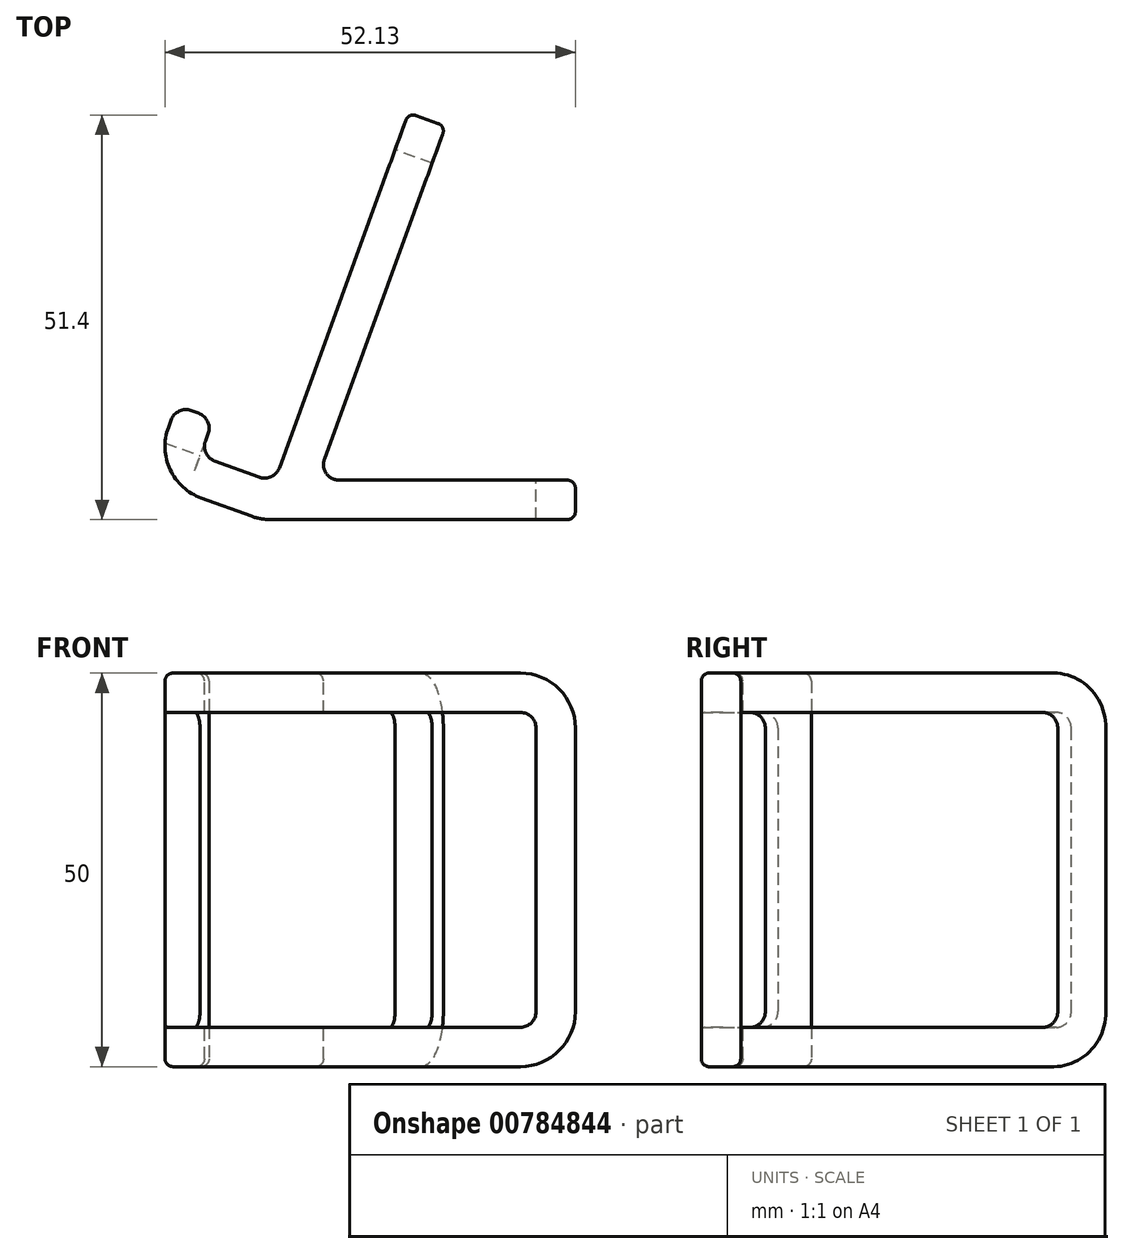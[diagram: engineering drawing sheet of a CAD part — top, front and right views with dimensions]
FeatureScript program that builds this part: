
annotation { "Feature Type Name" : "Feature", "Feature Type Description" : "" }
export const myFeature = defineFeature(function(context is Context, id is Id, definition is map)
    precondition{}
    {
        {
            var Q0;
            Q0=qCreatedBy(makeId("Top.planeOp"),FACE);
            var sketch = newSketch(context, id + "F0", { "sketchPlane" : qUnion([Q0])});
            skLineSegment(sketch, "E0", {"start": v(17.1, 46.98) * mm, "end": v(0, 0) * mm});
            skLineSegment(sketch, "E1", {"start": v(0, 0) * mm, "end": v(-9.4, 3.42) * mm});
            skLineSegment(sketch, "E2", {"start": v(38.29, -4.7) * mm, "end": v(38.29, 0.3) * mm});
            skLineSegment(sketch, "E3", {"start": v(38.29, 0.3) * mm, "end": v(5.43, 0.3) * mm});
            skLineSegment(sketch, "E4", {"start": v(5.43, 0.3) * mm, "end": v(21.8, 45.27) * mm});
            skLineSegment(sketch, "E5", {"start": v(21.8, 45.27) * mm, "end": v(17.1, 46.98) * mm});
            skLineSegment(sketch, "E6", {"start": v(-9.4, 3.42) * mm, "end": v(-7.69, 8.12) * mm});
            skLineSegment(sketch, "E7", {"start": v(-7.69, 8.12) * mm, "end": v(-12.39, 9.83) * mm});
            skLineSegment(sketch, "E8", {"start": v(-12.39, 9.83) * mm, "end": v(-15.8, 0.43) * mm});
            skLineSegment(sketch, "E9", {"start": v(-15.8, 0.43) * mm, "end": v(-1.71, -4.7) * mm});
            skLineSegment(sketch, "E10", {"start": v(-1.71, -4.7) * mm, "end": v(38.29, -4.7) * mm});
            skLineSegment(sketch, "E11", {"start": v(0, 0) * mm, "end": v(0, 50) * mm, "construction": true});
            skLineSegment(sketch, "E12", {"start": v(0, 0) * mm, "end": v(54.72, 150.35) * mm, "construction": true});
            skPoint(sketch, "E13", {"position": v(27.36, 75.18) * mm});
            skLineSegment(sketch, "E14", {"start": v(27.36, 75.18) * mm, "end": v(27.36, -4.7) * mm, "construction": true});
            skSolve(sketch);
        }
        {
            var Q0;
            Q0=makeQuery(id+"F0.imprint","IMPRINT",FACE,{"disambiguationData":[TD([[makeQuery(id+"F0.imprint","IMPRINT",EDGE,{"derivedFrom":sQuery(id+"F0.wireOp",EDGE,"E0")}),1.0]])]});
            extrude(context, id + "F1", {"entities" : qUnion([Q0]), "depth" : 50 * mm, "offsetDistance" : 25 * mm});
        }
        {
            var Q0;
            Q0=makeQuery(id+"F1.opExtrude","SWEPT_FACE",FACE,{"disambiguationData":[OSD([sQuery(id+"F0.wireOp",EDGE,"E0")])]});
            var sketch = newSketch(context, id + "F2", { "sketchPlane" : qUnion([Q0])});
            skLineSegment(sketch, "E15.bottom", {"start": v(-45, 5) * mm, "end": v(5, 5) * mm});
            skLineSegment(sketch, "E15.top", {"start": v(-45, 45) * mm, "end": v(5, 45) * mm});
            skLineSegment(sketch, "E15.left", {"start": v(-45, 5) * mm, "end": v(-45, 45) * mm});
            skLineSegment(sketch, "E15.right", {"start": v(5, 5) * mm, "end": v(5, 45) * mm});
            skSolve(sketch);
        }
        {
            var Q0;
            Q0=makeQuery(id+"F1.opExtrude","SWEPT_FACE",FACE,{"disambiguationData":[OSD([sQuery(id+"F0.wireOp",EDGE,"E3")])]});
            var sketch = newSketch(context, id + "F3", { "sketchPlane" : qUnion([Q0])});
            skLineSegment(sketch, "E16.bottom", {"start": v(-33.29, 5) * mm, "end": v(-5.43, 5) * mm});
            skLineSegment(sketch, "E16.top", {"start": v(-33.29, 45) * mm, "end": v(-5.43, 45) * mm});
            skLineSegment(sketch, "E16.left", {"start": v(-33.29, 5) * mm, "end": v(-33.29, 45) * mm});
            skLineSegment(sketch, "E16.right", {"start": v(-5.43, 5) * mm, "end": v(-5.43, 45) * mm});
            skSolve(sketch);
        }
        {
            var Q0;
            Q0=makeQuery(id+"F1.opExtrude","SWEPT_FACE",FACE,{"disambiguationData":[OSD([sQuery(id+"F0.wireOp",EDGE,"E1")])]});
            var sketch = newSketch(context, id + "F4", { "sketchPlane" : qUnion([Q0])});
            skLineSegment(sketch, "E17.bottom", {"start": v(20, 5) * mm, "end": v(-10, 5) * mm});
            skLineSegment(sketch, "E17.top", {"start": v(20, 45) * mm, "end": v(-10, 45) * mm});
            skLineSegment(sketch, "E17.left", {"start": v(20, 5) * mm, "end": v(20, 45) * mm});
            skLineSegment(sketch, "E17.right", {"start": v(-10, 5) * mm, "end": v(-10, 45) * mm});
            skSolve(sketch);
        }
        {
            var Q0;
            Q0=makeQuery(id+"F3.imprint","IMPRINT",FACE,{"disambiguationData":[TD([[makeQuery(id+"F3.imprint","IMPRINT",EDGE,{"derivedFrom":sQuery(id+"F3.wireOp",EDGE,"E16.bottom")}),1.0]])]});
            extrude(context, id + "F5", {"entities" : qUnion([Q0]), "operationType" : NewBodyOperationType.REMOVE, "endBound" : BoundingType.THROUGH_ALL, "oppositeDirection" : true, "depth" : 26.6 * mm, "offsetDistance" : 25 * mm});
        }
        {
            var Q0;
            Q0=makeQuery(id+"F4.imprint","IMPRINT",FACE,{"disambiguationData":[TD([[makeQuery(id+"F4.imprint","IMPRINT",EDGE,{"derivedFrom":sQuery(id+"F4.wireOp",EDGE,"E17.bottom")}),-1.0]])]});
            extrude(context, id + "F6", {"entities" : qUnion([Q0]), "operationType" : NewBodyOperationType.REMOVE, "endBound" : BoundingType.THROUGH_ALL, "oppositeDirection" : true, "depth" : 25 * mm, "offsetDistance" : 25 * mm});
        }
        {
            var Q0;
            Q0=makeQuery(id+"F2.imprint","IMPRINT",FACE,{"disambiguationData":[TD([[makeQuery(id+"F2.imprint","IMPRINT",EDGE,{"derivedFrom":sQuery(id+"F2.wireOp",EDGE,"E15.bottom")}),1.0]])]});
            var Q1;
            Q1=makeQuery(id+"F1.opExtrude","SWEPT_FACE",FACE,{"disambiguationData":[OSD([sQuery(id+"F0.wireOp",EDGE,"E4")])]});
            extrude(context, id + "F7", {"entities" : qUnion([Q0]), "operationType" : NewBodyOperationType.REMOVE, "oppositeDirection" : true, "depth" : 21.25 * mm, "endBoundEntityFace" : qUnion([Q1]), "offsetDistance" : 25 * mm});
        }
        {
            var Q0;
            {var subQ0=sQuery(id+"F0.wireOp",EDGE,"E9");var subQ1=sQuery(id+"F0.wireOp",EDGE,"E8");Q0=makeQuery(id+"F6.boolean.opBoolean","SPLIT",EDGE,{"disambiguationData":[TD([makeQuery(id+"F5.boolean.opBoolean","COPY",FACE,{"derivedFrom":makeQuery(id+"F5.opExtrude","SWEPT_FACE",FACE,{"disambiguationData":[OSD([sQuery(id+"F3.wireOp",EDGE,"E16.top")])]})})])],"derivedFrom":makeQuery(id+"F1.opExtrude","SWEPT_EDGE",EDGE,{"disambiguationData":[OSD([subQ1,subQ0])]})});}
            var Q1;
            {var subQ0=sQuery(id+"F0.wireOp",EDGE,"E8");var subQ1=sQuery(id+"F0.wireOp",EDGE,"E9");Q1=makeQuery(id+"F6.boolean.opBoolean","SPLIT",EDGE,{"disambiguationData":[TD([makeQuery(id+"F5.boolean.opBoolean","COPY",FACE,{"derivedFrom":makeQuery(id+"F5.opExtrude","SWEPT_FACE",FACE,{"disambiguationData":[OSD([sQuery(id+"F3.wireOp",EDGE,"E16.bottom")])]})})])],"derivedFrom":makeQuery(id+"F1.opExtrude","SWEPT_EDGE",EDGE,{"disambiguationData":[OSD([subQ0,subQ1])]})});}
            var Q2;
            {var subQ0=sQuery(id+"F0.wireOp",EDGE,"E9");var subQ1=sQuery(id+"F0.wireOp",EDGE,"E10");Q2=makeQuery(id+"F6.boolean.opBoolean","SPLIT",EDGE,{"disambiguationData":[TD([makeQuery(id+"F5.boolean.opBoolean","COPY",FACE,{"derivedFrom":makeQuery(id+"F5.opExtrude","SWEPT_FACE",FACE,{"disambiguationData":[OSD([sQuery(id+"F3.wireOp",EDGE,"E16.top")])]})})])],"derivedFrom":makeQuery(id+"F1.opExtrude","SWEPT_EDGE",EDGE,{"disambiguationData":[OSD([subQ0,subQ1])]})});}
            var Q3;
            {var subQ0=sQuery(id+"F0.wireOp",EDGE,"E10");var subQ1=sQuery(id+"F0.wireOp",EDGE,"E9");Q3=makeQuery(id+"F6.boolean.opBoolean","SPLIT",EDGE,{"disambiguationData":[TD([makeQuery(id+"F5.boolean.opBoolean","COPY",FACE,{"derivedFrom":makeQuery(id+"F5.opExtrude","SWEPT_FACE",FACE,{"disambiguationData":[OSD([sQuery(id+"F3.wireOp",EDGE,"E16.bottom")])]})})])],"derivedFrom":makeQuery(id+"F1.opExtrude","SWEPT_EDGE",EDGE,{"disambiguationData":[OSD([subQ1,subQ0])]})});}
            var Q4;
            Q4=makeQuery(id+"F1.opExtrude","CAP_EDGE",EDGE,{"disambiguationData":[OSD([sQuery(id+"F0.wireOp",EDGE,"E5")])],"isStart":true});
            var Q5;
            Q5=makeQuery(id+"F1.opExtrude","CAP_EDGE",EDGE,{"disambiguationData":[OSD([sQuery(id+"F0.wireOp",EDGE,"E5")])],"isStart":false});
            var Q6;
            Q6=makeQuery(id+"F1.opExtrude","CAP_EDGE",EDGE,{"disambiguationData":[OSD([sQuery(id+"F0.wireOp",EDGE,"E2")])],"isStart":true});
            var Q7;
            Q7=makeQuery(id+"F1.opExtrude","CAP_EDGE",EDGE,{"disambiguationData":[OSD([sQuery(id+"F0.wireOp",EDGE,"E2")])],"isStart":false});
            fillet(context, id + "F8", {"entities" : qUnion([Q0, Q1, Q2, Q3, Q4, Q5, Q6, Q7]), "radius" : 7 * mm, "allowEdgeOverflow" : false});
        }
        {
            var Q0;
            Q0=makeQuery(id+"F7.boolean.opBoolean","COPY",EDGE,{"derivedFrom":makeQuery(id+"F7.opExtrude","SWEPT_EDGE",EDGE,{"disambiguationData":[OSD([sQuery(id+"F2.wireOp",EDGE,"E15.top"),sQuery(id+"F2.wireOp",EDGE,"E15.left")])]})});
            var Q1;
            Q1=makeQuery(id+"F7.boolean.opBoolean","COPY",EDGE,{"derivedFrom":makeQuery(id+"F7.opExtrude","SWEPT_EDGE",EDGE,{"disambiguationData":[OSD([sQuery(id+"F2.wireOp",EDGE,"E15.bottom"),sQuery(id+"F2.wireOp",EDGE,"E15.left")])]})});
            var Q2;
            Q2=makeQuery(id+"F5.boolean.opBoolean","COPY",EDGE,{"derivedFrom":makeQuery(id+"F5.opExtrude","SWEPT_EDGE",EDGE,{"disambiguationData":[OSD([sQuery(id+"F3.wireOp",EDGE,"E16.bottom"),sQuery(id+"F3.wireOp",EDGE,"E16.left")])]})});
            var Q3;
            Q3=makeQuery(id+"F5.boolean.opBoolean","COPY",EDGE,{"derivedFrom":makeQuery(id+"F5.opExtrude","SWEPT_EDGE",EDGE,{"disambiguationData":[OSD([sQuery(id+"F3.wireOp",EDGE,"E16.top"),sQuery(id+"F3.wireOp",EDGE,"E16.left")])]})});
            var Q4;
            {var subQ0=sQuery(id+"F0.wireOp",EDGE,"E6");var subQ1=makeQuery(id+"F1.opExtrude","SWEPT_FACE",FACE,{"disambiguationData":[OSD([subQ0])]});var subQ2=sQuery(id+"F0.wireOp",EDGE,"E1");var subQ3=makeQuery(id+"F1.opExtrude","SWEPT_FACE",FACE,{"disambiguationData":[OSD([subQ2])]});Q4=makeQuery(id+"F6.boolean.opBoolean","SPLIT",EDGE,{"disambiguationData":[topologyDisambiguationEdgeConnected([subQ3,subQ1]),TD([makeQuery(id+"F5.boolean.opBoolean","COPY",FACE,{"derivedFrom":makeQuery(id+"F5.opExtrude","SWEPT_FACE",FACE,{"disambiguationData":[OSD([sQuery(id+"F3.wireOp",EDGE,"E16.bottom")])]})})])],"derivedFrom":makeQuery(id+"F1.opExtrude","SWEPT_EDGE",EDGE,{"disambiguationData":[OSD([subQ2,subQ0])]})});}
            var Q5;
            {var subQ0=sQuery(id+"F0.wireOp",EDGE,"E6");var subQ1=makeQuery(id+"F1.opExtrude","SWEPT_FACE",FACE,{"disambiguationData":[OSD([subQ0])]});var subQ2=sQuery(id+"F0.wireOp",EDGE,"E1");var subQ3=makeQuery(id+"F1.opExtrude","SWEPT_FACE",FACE,{"disambiguationData":[OSD([subQ2])]});Q5=makeQuery(id+"F6.boolean.opBoolean","SPLIT",EDGE,{"disambiguationData":[topologyDisambiguationEdgeConnected([subQ3,subQ1]),TD([makeQuery(id+"F5.boolean.opBoolean","COPY",FACE,{"derivedFrom":makeQuery(id+"F5.opExtrude","SWEPT_FACE",FACE,{"disambiguationData":[OSD([sQuery(id+"F3.wireOp",EDGE,"E16.top")])]})})])],"derivedFrom":makeQuery(id+"F1.opExtrude","SWEPT_EDGE",EDGE,{"disambiguationData":[OSD([subQ2,subQ0])]})});}
            var Q6;
            {var subQ0=sQuery(id+"F0.wireOp",EDGE,"E0");var subQ1=makeQuery(id+"F1.opExtrude","SWEPT_FACE",FACE,{"disambiguationData":[OSD([subQ0])]});var subQ2=sQuery(id+"F0.wireOp",EDGE,"E1");var subQ3=makeQuery(id+"F1.opExtrude","SWEPT_FACE",FACE,{"disambiguationData":[OSD([subQ2])]});Q6=makeQuery(id+"F6.boolean.opBoolean","SPLIT",EDGE,{"disambiguationData":[topologyDisambiguationEdgeConnected([subQ1,subQ3]),TD([makeQuery(id+"F5.boolean.opBoolean","COPY",FACE,{"derivedFrom":makeQuery(id+"F5.opExtrude","SWEPT_FACE",FACE,{"disambiguationData":[OSD([sQuery(id+"F3.wireOp",EDGE,"E16.top")])]})})])],"derivedFrom":makeQuery(id+"F1.opExtrude","SWEPT_EDGE",EDGE,{"disambiguationData":[OSD([subQ0,subQ2])]})});}
            var Q7;
            {var subQ0=sQuery(id+"F0.wireOp",EDGE,"E1");var subQ1=makeQuery(id+"F1.opExtrude","SWEPT_FACE",FACE,{"disambiguationData":[OSD([subQ0])]});var subQ3=sQuery(id+"F0.wireOp",EDGE,"E0");var subQ4=makeQuery(id+"F1.opExtrude","SWEPT_FACE",FACE,{"disambiguationData":[OSD([subQ3])]});Q7=makeQuery(id+"F6.boolean.opBoolean","SPLIT",EDGE,{"disambiguationData":[topologyDisambiguationEdgeConnected([subQ4,subQ1]),TD([makeQuery(id+"F5.boolean.opBoolean","COPY",FACE,{"derivedFrom":makeQuery(id+"F5.opExtrude","SWEPT_FACE",FACE,{"disambiguationData":[OSD([sQuery(id+"F3.wireOp",EDGE,"E16.bottom")])]})})])],"derivedFrom":makeQuery(id+"F1.opExtrude","SWEPT_EDGE",EDGE,{"disambiguationData":[OSD([subQ3,subQ0])]})});}
            var Q8;
            {var subQ0=sQuery(id+"F0.wireOp",EDGE,"E4");var subQ1=sQuery(id+"F0.wireOp",EDGE,"E3");Q8=makeQuery(id+"F5.boolean.opBoolean","SPLIT",EDGE,{"disambiguationData":[TD([makeQuery(id+"F5.opExtrude","SWEPT_FACE",FACE,{"disambiguationData":[OSD([sQuery(id+"F3.wireOp",EDGE,"E16.bottom")])]})])],"derivedFrom":makeQuery(id+"F1.opExtrude","SWEPT_EDGE",EDGE,{"disambiguationData":[OSD([subQ1,subQ0])]})});}
            var Q9;
            {var subQ0=sQuery(id+"F0.wireOp",EDGE,"E4");var subQ1=sQuery(id+"F0.wireOp",EDGE,"E3");Q9=makeQuery(id+"F5.boolean.opBoolean","SPLIT",EDGE,{"disambiguationData":[TD([makeQuery(id+"F5.opExtrude","SWEPT_FACE",FACE,{"disambiguationData":[OSD([sQuery(id+"F3.wireOp",EDGE,"E16.top")])]})])],"derivedFrom":makeQuery(id+"F1.opExtrude","SWEPT_EDGE",EDGE,{"disambiguationData":[OSD([subQ1,subQ0])]})});}
            var Q10;
            Q10=makeQuery(id+"F1.opExtrude","SWEPT_EDGE",EDGE,{"disambiguationData":[OSD([sQuery(id+"F0.wireOp",EDGE,"E7"),sQuery(id+"F0.wireOp",EDGE,"E8")])]});
            var Q11;
            Q11=makeQuery(id+"F1.opExtrude","SWEPT_EDGE",EDGE,{"disambiguationData":[OSD([sQuery(id+"F0.wireOp",EDGE,"E6"),sQuery(id+"F0.wireOp",EDGE,"E7")])]});
            fillet(context, id + "F9", {"entities" : qUnion([Q0, Q1, Q2, Q3, Q4, Q5, Q6, Q7, Q8, Q9, Q10, Q11]), "radius" : 2 * mm, "tangentPropagation" : true, "allowEdgeOverflow" : false});
        }
        {
            var Q0;
            {var subQ0=makeQuery(id+"F5.boolean.opBoolean","COPY",FACE,{"derivedFrom":makeQuery(id+"F5.opExtrude","SWEPT_FACE",FACE,{"disambiguationData":[OSD([sQuery(id+"F3.wireOp",EDGE,"E16.top")])]})});var subQ1=sQuery(id+"F4.wireOp",EDGE,"E17.top");var subQ2=makeQuery(id+"F6.opExtrude","CAP_FACE",FACE,{"disambiguationData":[OSD([sQuery(id+"F4.wireOp",EDGE,"E17.bottom"),subQ1,sQuery(id+"F4.wireOp",EDGE,"E17.left"),sQuery(id+"F4.wireOp",EDGE,"E17.right")])],"isStart":true});var subQ3=makeQuery(id+"F6.opExtrude","SWEPT_FACE",FACE,{"disambiguationData":[OSD([subQ1])]});Q0=makeQuery(id+"F6.boolean.opBoolean","COPY",EDGE,{"disambiguationData":[topologyDisambiguationEdgeConnected([subQ0,subQ2,subQ3]),TD([makeQuery(id+"F1.opExtrude","SWEPT_FACE",FACE,{"disambiguationData":[OSD([sQuery(id+"F0.wireOp",EDGE,"E6")])]})])],"derivedFrom":makeQuery(id+"F6.opExtrude","CAP_EDGE",EDGE,{"disambiguationData":[OSD([subQ1])],"isStart":true})});}
            var Q1;
            {var subQ0=makeQuery(id+"F5.boolean.opBoolean","COPY",FACE,{"derivedFrom":makeQuery(id+"F5.opExtrude","SWEPT_FACE",FACE,{"disambiguationData":[OSD([sQuery(id+"F3.wireOp",EDGE,"E16.bottom")])]})});var subQ1=sQuery(id+"F4.wireOp",EDGE,"E17.bottom");var subQ2=makeQuery(id+"F6.opExtrude","SWEPT_FACE",FACE,{"disambiguationData":[OSD([subQ1])]});var subQ3=makeQuery(id+"F6.opExtrude","CAP_FACE",FACE,{"disambiguationData":[OSD([subQ1,sQuery(id+"F4.wireOp",EDGE,"E17.top"),sQuery(id+"F4.wireOp",EDGE,"E17.left"),sQuery(id+"F4.wireOp",EDGE,"E17.right")])],"isStart":true});Q1=makeQuery(id+"F6.boolean.opBoolean","COPY",EDGE,{"disambiguationData":[topologyDisambiguationEdgeConnected([subQ0,subQ2,subQ3]),TD([makeQuery(id+"F1.opExtrude","SWEPT_FACE",FACE,{"disambiguationData":[OSD([sQuery(id+"F0.wireOp",EDGE,"E6")])]})])],"derivedFrom":makeQuery(id+"F6.opExtrude","CAP_EDGE",EDGE,{"disambiguationData":[OSD([subQ1])],"isStart":true})});}
            var Q2;
            {var subQ0=sQuery(id+"F4.wireOp",EDGE,"E17.top");Q2=makeQuery(id+"F9.opFillet","TWEAK_EDGE",EDGE,{"derivedFrom":[makeQuery(id+"F6.boolean.opBoolean","TWEAK_VERTEX",VERTEX,{"derivedFrom":[makeQuery(id+"F1.opExtrude","SWEPT_FACE",FACE,{"disambiguationData":[OSD([sQuery(id+"F0.wireOp",EDGE,"E1")])]}),makeQuery(id+"F1.opExtrude","SWEPT_FACE",FACE,{"disambiguationData":[OSD([sQuery(id+"F0.wireOp",EDGE,"E6")])]}),makeQuery(id+"F5.boolean.opBoolean","COPY",FACE,{"derivedFrom":makeQuery(id+"F5.opExtrude","SWEPT_FACE",FACE,{"disambiguationData":[OSD([sQuery(id+"F3.wireOp",EDGE,"E16.top")])]})}),makeQuery(id+"F6.opExtrude","CAP_FACE",FACE,{"disambiguationData":[OSD([sQuery(id+"F4.wireOp",EDGE,"E17.bottom"),subQ0,sQuery(id+"F4.wireOp",EDGE,"E17.left"),sQuery(id+"F4.wireOp",EDGE,"E17.right")])],"isStart":true}),makeQuery(id+"F6.opExtrude","SWEPT_FACE",FACE,{"disambiguationData":[OSD([subQ0])]})]})]});}
            var Q3;
            {var subQ0=sQuery(id+"F4.wireOp",EDGE,"E17.bottom");Q3=makeQuery(id+"F9.opFillet","TWEAK_EDGE",EDGE,{"derivedFrom":[makeQuery(id+"F6.boolean.opBoolean","TWEAK_VERTEX",VERTEX,{"derivedFrom":[makeQuery(id+"F1.opExtrude","SWEPT_FACE",FACE,{"disambiguationData":[OSD([sQuery(id+"F0.wireOp",EDGE,"E1")])]}),makeQuery(id+"F1.opExtrude","SWEPT_FACE",FACE,{"disambiguationData":[OSD([sQuery(id+"F0.wireOp",EDGE,"E6")])]}),makeQuery(id+"F5.boolean.opBoolean","COPY",FACE,{"derivedFrom":makeQuery(id+"F5.opExtrude","SWEPT_FACE",FACE,{"disambiguationData":[OSD([sQuery(id+"F3.wireOp",EDGE,"E16.bottom")])]})}),makeQuery(id+"F6.opExtrude","SWEPT_FACE",FACE,{"disambiguationData":[OSD([subQ0])]}),makeQuery(id+"F6.opExtrude","CAP_FACE",FACE,{"disambiguationData":[OSD([subQ0,sQuery(id+"F4.wireOp",EDGE,"E17.top"),sQuery(id+"F4.wireOp",EDGE,"E17.left"),sQuery(id+"F4.wireOp",EDGE,"E17.right")])],"isStart":true})]})]});}
            fillet(context, id + "F10", {"entities" : qUnion([Q0, Q1, Q2, Q3]), "radius" : 2 * mm, "tangentPropagation" : true, "allowEdgeOverflow" : false});
        }
        {
            var Q0;
            Q0=makeQuery(id+"F5.boolean.opBoolean","COPY",EDGE,{"derivedFrom":makeQuery(id+"F5.opExtrude","CAP_EDGE",EDGE,{"disambiguationData":[OSD([sQuery(id+"F3.wireOp",EDGE,"E16.left")])],"isStart":true})});
            var Q1;
            Q1=makeQuery(id+"F1.opExtrude","SWEPT_EDGE",EDGE,{"disambiguationData":[OSD([sQuery(id+"F0.wireOp",EDGE,"E2"),sQuery(id+"F0.wireOp",EDGE,"E3")])]});
            var Q2;
            Q2=makeQuery(id+"F1.opExtrude","CAP_EDGE",EDGE,{"disambiguationData":[OSD([sQuery(id+"F0.wireOp",EDGE,"E0")])],"isStart":true});
            var Q3;
            Q3=makeQuery(id+"F6.boolean.opBoolean","INTERSECT",EDGE,{"derivedFrom":[makeQuery(id+"F1.opExtrude","SWEPT_FACE",FACE,{"disambiguationData":[OSD([sQuery(id+"F0.wireOp",EDGE,"E10")])]}),makeQuery(id+"F6.opExtrude","SWEPT_FACE",FACE,{"disambiguationData":[OSD([sQuery(id+"F4.wireOp",EDGE,"E17.bottom")])]})]});
            var Q4;
            Q4=makeQuery(id+"F7.boolean.opBoolean","COPY",EDGE,{"derivedFrom":makeQuery(id+"F7.opExtrude","CAP_EDGE",EDGE,{"disambiguationData":[OSD([sQuery(id+"F2.wireOp",EDGE,"E15.bottom")])],"isStart":true})});
            var Q5;
            {var subQ0=sQuery(id+"F0.wireOp",EDGE,"E6");Q5=makeQuery(id+"F6.boolean.opBoolean","SPLIT",EDGE,{"disambiguationData":[topologyDisambiguationEdgeConnected([makeQuery(id+"F1.opExtrude","SWEPT_FACE",FACE,{"disambiguationData":[OSD([subQ0])]}),makeQuery(id+"F6.opExtrude","CAP_FACE",FACE,{"disambiguationData":[OSD([sQuery(id+"F4.wireOp",EDGE,"E17.bottom"),sQuery(id+"F4.wireOp",EDGE,"E17.top"),sQuery(id+"F4.wireOp",EDGE,"E17.left"),sQuery(id+"F4.wireOp",EDGE,"E17.right")])],"isStart":true})])],"derivedFrom":makeQuery(id+"F1.opExtrude","SWEPT_EDGE",EDGE,{"disambiguationData":[OSD([sQuery(id+"F0.wireOp",EDGE,"E1"),subQ0])]})});}
            fillet(context, id + "F11", {"entities" : qUnion([Q0, Q1, Q2, Q3, Q4, Q5]), "radius" : 1 * mm, "tangentPropagation" : true, "allowEdgeOverflow" : false});
        }
    });
